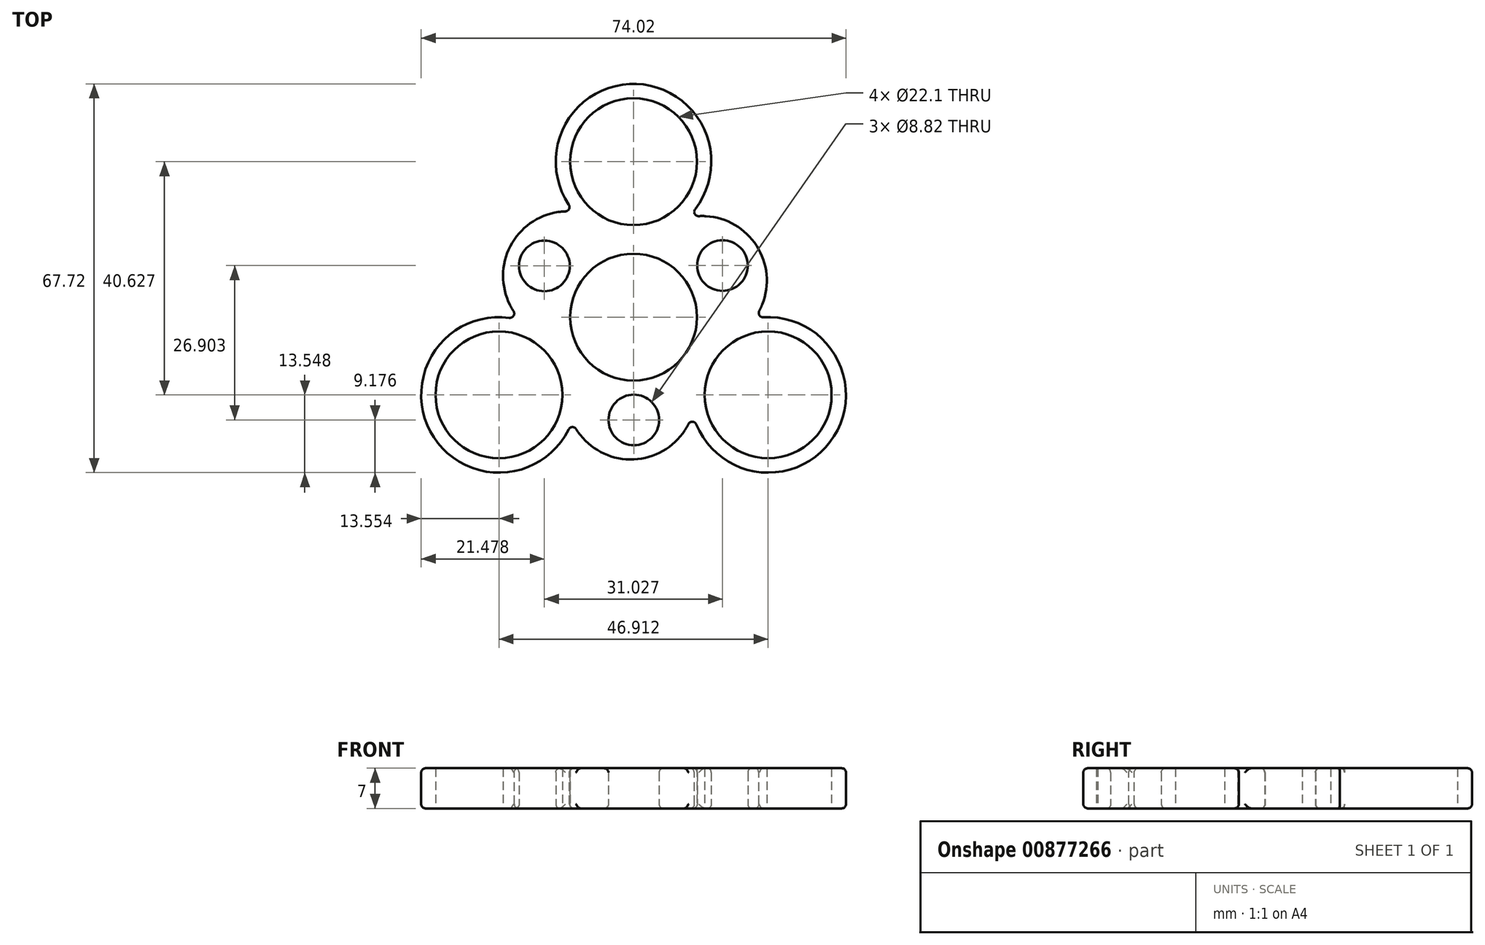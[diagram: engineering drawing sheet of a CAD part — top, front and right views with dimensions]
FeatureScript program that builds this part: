
annotation { "Feature Type Name" : "Feature", "Feature Type Description" : "" }
export const myFeature = defineFeature(function(context is Context, id is Id, definition is map)
    precondition{}
    {
        {
            var Q0;
            Q0=qCreatedBy(makeId("Top.planeOp"),FACE);
            var sketch = newSketch(context, id + "F0", { "sketchPlane" : qUnion([Q0])});
            skCircle(sketch, "E0", {"center": v(0, 0) * mm, "radius": 11.05 * mm});
            skCircle(sketch, "E1", {"center": v(0, 27.08) * mm, "radius": 11.05 * mm});
            skArc(sketch, "E2", {"start": v(9.39, 17.31) * mm, "mid": v(0.73, 40.61) * mm, "end": v(-10.38, 18.38) * mm});
            skCircle(sketch, "E3.1.0", {"center": v(-23.46, -13.54) * mm, "radius": 11.05 * mm});
            skArc(sketch, "E3.1.1", {"start": v(-19.69, -0.53) * mm, "mid": v(-35.54, -19.68) * mm, "end": v(-10.72, -18.18) * mm});
            skCircle(sketch, "E3.2.0", {"center": v(23.46, -13.54) * mm, "radius": 11.05 * mm});
            skArc(sketch, "E3.2.1", {"start": v(10.3, -16.78) * mm, "mid": v(34.8, -20.94) * mm, "end": v(21.1, -0.2) * mm});
            skArc(sketch, "E4.trimOffspring", {"start": v(-10.38, 18.38) * mm, "mid": v(-21.58, 12.15) * mm, "end": v(-19.69, -0.53) * mm});
            skArc(sketch, "E5.trimOffspring", {"start": v(-10.72, -18.18) * mm, "mid": v(0.27, -24.77) * mm, "end": v(10.3, -16.78) * mm});
            skArc(sketch, "E6.trimOffspring", {"start": v(21.1, -0.2) * mm, "mid": v(21.31, 12.62) * mm, "end": v(9.39, 17.31) * mm});
            skCircle(sketch, "E7", {"center": v(-15.53, 8.92) * mm, "radius": 4.41 * mm});
            skCircle(sketch, "E8.1.0", {"center": v(0.04, -17.91) * mm, "radius": 4.41 * mm});
            skCircle(sketch, "E8.2.0", {"center": v(15.5, 8.99) * mm, "radius": 4.41 * mm});
            skSolve(sketch);
        }
        {
            var Q0;
            Q0 = qSketchRegion(id + "F0", true);
            extrude(context, id + "F1", {"entities" : qUnion([Q0]), "depth" : 7 * mm, "offsetDistance" : 25 * mm});
        }
        {
            var Q0;
            Q0=makeQuery(id+"F1.opExtrude","SWEPT_FACE",FACE,{"disambiguationData":[OSD([sQuery(id+"F0.wireOp",EDGE,"E3.2.1")])]});
            var Q1;
            Q1=makeQuery(id+"F1.opExtrude","SWEPT_FACE",FACE,{"disambiguationData":[OSD([sQuery(id+"F0.wireOp",EDGE,"E3.1.1")])]});
            var Q2;
            Q2=makeQuery(id+"F1.opExtrude","SWEPT_FACE",FACE,{"disambiguationData":[OSD([sQuery(id+"F0.wireOp",EDGE,"E2")])]});
            var Q3;
            Q3=makeQuery(id+"F1.opExtrude","CAP_EDGE",EDGE,{"disambiguationData":[OSD([sQuery(id+"F0.wireOp",EDGE,"E8.1.0")])],"isStart":false});
            var Q4;
            Q4=makeQuery(id+"F1.opExtrude","SWEPT_FACE",FACE,{"disambiguationData":[OSD([sQuery(id+"F0.wireOp",EDGE,"E8.1.0")])]});
            var Q5;
            Q5=makeQuery(id+"F1.opExtrude","SWEPT_FACE",FACE,{"disambiguationData":[OSD([sQuery(id+"F0.wireOp",EDGE,"E7")])]});
            var Q6;
            Q6=makeQuery(id+"F1.opExtrude","SWEPT_FACE",FACE,{"disambiguationData":[OSD([sQuery(id+"F0.wireOp",EDGE,"E8.2.0")])]});
            fillet(context, id + "F2", {"entities" : qUnion([Q0, Q1, Q2, Q3, Q4, Q5, Q6]), "radius" : 0.75 * mm, "tangentPropagation" : true, "allowEdgeOverflow" : false});
        }
    });
